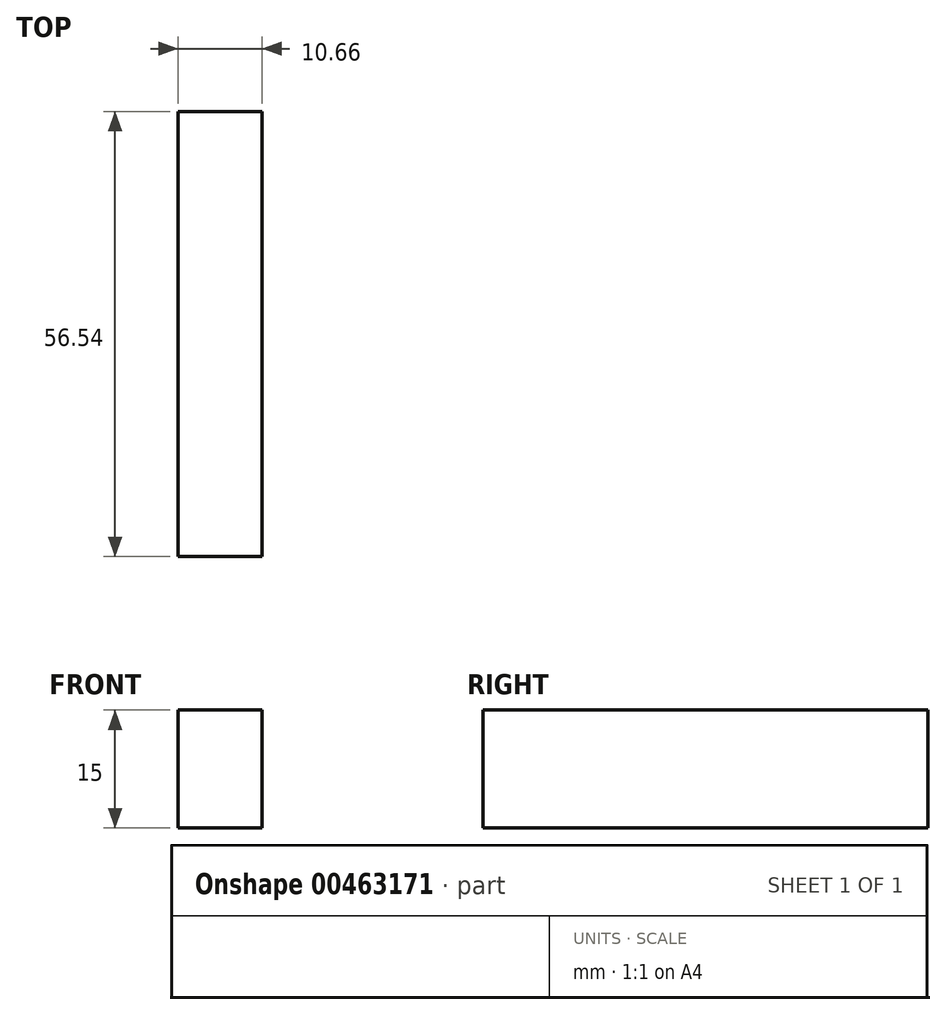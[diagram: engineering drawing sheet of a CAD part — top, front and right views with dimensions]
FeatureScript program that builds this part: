
annotation { "Feature Type Name" : "Feature", "Feature Type Description" : "" }
export const myFeature = defineFeature(function(context is Context, id is Id, definition is map)
    precondition{}
    {
        {
            var Q0;
            Q0=qCreatedBy(makeId("Top.planeOp"),FACE);
            var sketch = newSketch(context, id + "F0", { "sketchPlane" : qUnion([Q0])});
            skLineSegment(sketch, "E0.bottom", {"start": v(5.33, -28.27) * mm, "end": v(-5.33, -28.27) * mm});
            skLineSegment(sketch, "E0.top", {"start": v(5.33, 28.27) * mm, "end": v(-5.33, 28.27) * mm});
            skLineSegment(sketch, "E0.left", {"start": v(5.33, -28.27) * mm, "end": v(5.33, 28.27) * mm});
            skLineSegment(sketch, "E0.right", {"start": v(-5.33, -28.27) * mm, "end": v(-5.33, 28.27) * mm});
            skPoint(sketch, "E0.middle", {"position": v(0, 0) * mm});
            skSolve(sketch);
        }
        {
            var Q0;
            Q0=makeQuery(id+"F0.imprint","IMPRINT",FACE,{"disambiguationData":[TD([[makeQuery(id+"F0.imprint","IMPRINT",EDGE,{"derivedFrom":sQuery(id+"F0.wireOp",EDGE,"E0.bottom")}),-1.0]])]});
            extrude(context, id + "F1", {"entities" : qUnion([Q0]), "depth" : 15 * mm});
        }
    });
